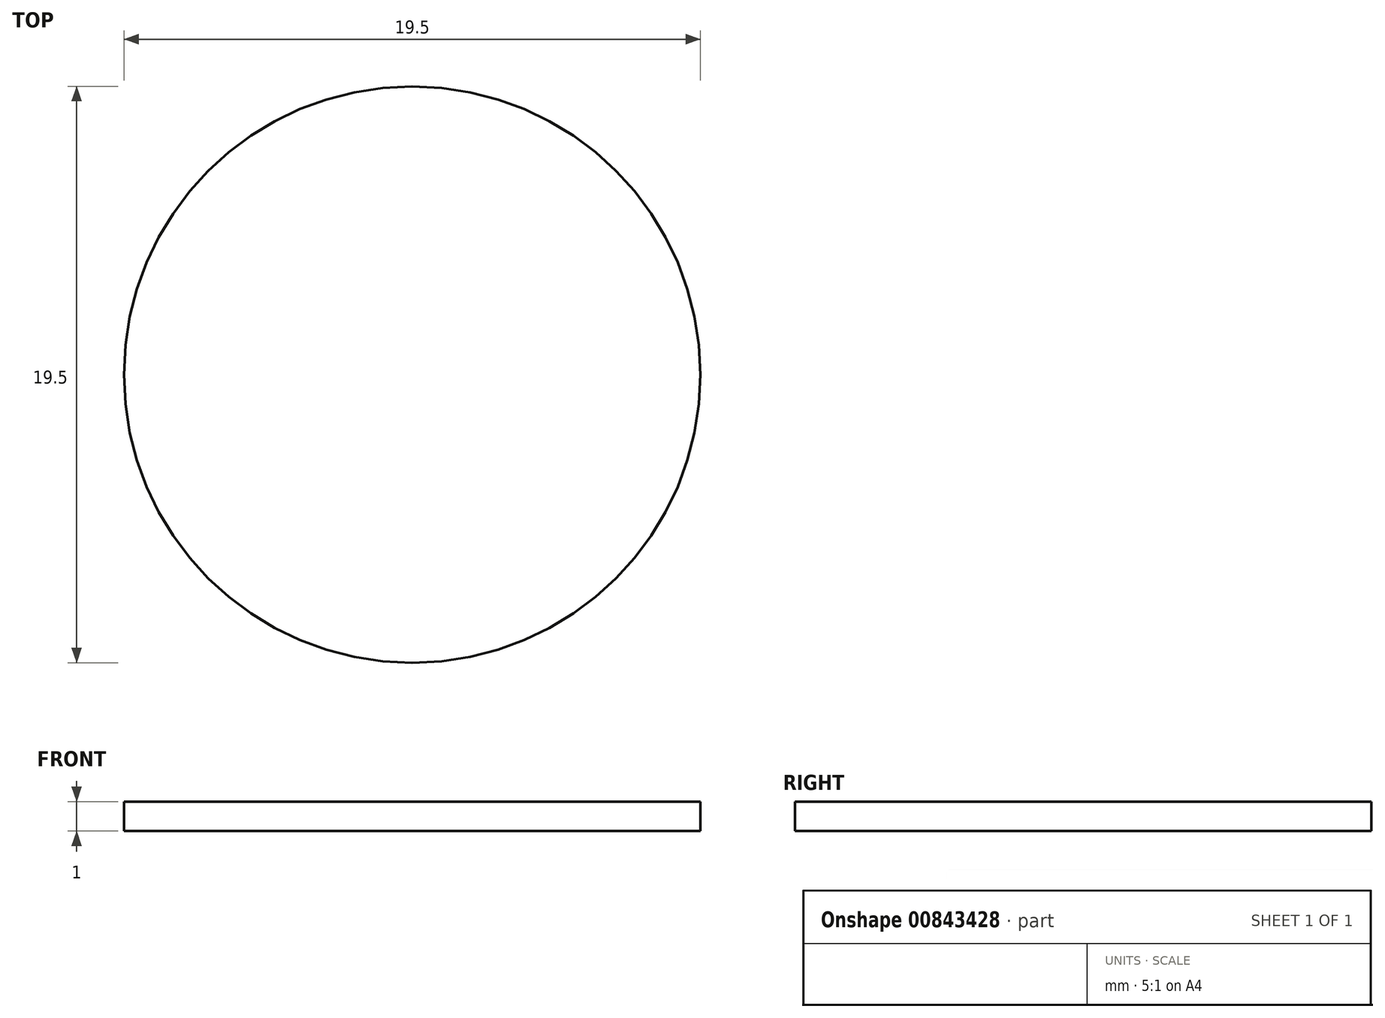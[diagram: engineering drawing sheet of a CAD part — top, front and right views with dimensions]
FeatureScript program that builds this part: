
annotation { "Feature Type Name" : "Feature", "Feature Type Description" : "" }
export const myFeature = defineFeature(function(context is Context, id is Id, definition is map)
    precondition{}
    {
        {
            var Q0;
            Q0=qCreatedBy(makeId("Top.planeOp"),FACE);
            var sketch = newSketch(context, id + "F0", { "sketchPlane" : qUnion([Q0])});
            skCircle(sketch, "E0", {"center": v(0, 0) * mm, "radius": 9.75 * mm});
            skSolve(sketch);
        }
        {
            var Q0;
            Q0 = qSketchRegion(id + "F0", true);
            extrude(context, id + "F1", {"entities" : qUnion([Q0]), "depth" : 1 * mm, "offsetDistance" : 25 * mm});
        }
    });
